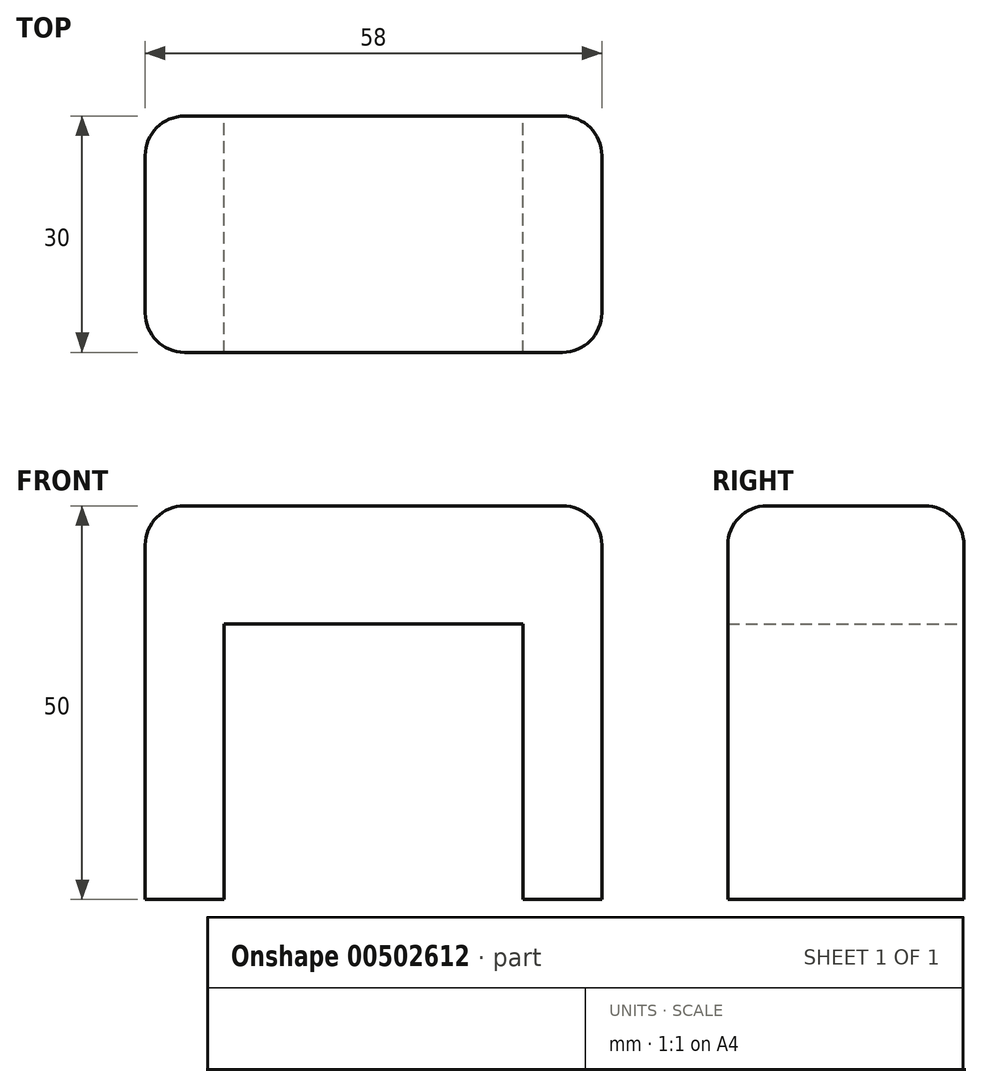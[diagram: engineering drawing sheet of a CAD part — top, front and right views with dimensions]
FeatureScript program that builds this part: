
annotation { "Feature Type Name" : "Feature", "Feature Type Description" : "" }
export const myFeature = defineFeature(function(context is Context, id is Id, definition is map)
    precondition{}
    {
        {
            var Q0;
            Q0=qCreatedBy(makeId("Front.planeOp"),FACE);
            var sketch = newSketch(context, id + "F0", { "sketchPlane" : qUnion([Q0])});
            skLineSegment(sketch, "E0.bottom", {"start": v(0, 0) * mm, "end": v(10, 0) * mm});
            skLineSegment(sketch, "E0.top", {"start": v(0, -50) * mm, "end": v(10, -50) * mm});
            skLineSegment(sketch, "E0.left", {"start": v(0, 0) * mm, "end": v(0, -50) * mm});
            skLineSegment(sketch, "E0.right", {"start": v(10, 0) * mm, "end": v(10, -50) * mm});
            skLineSegment(sketch, "E1.bottom", {"start": v(10, 0) * mm, "end": v(48, 0) * mm});
            skLineSegment(sketch, "E1.top", {"start": v(10, -15) * mm, "end": v(48, -15) * mm});
            skLineSegment(sketch, "E1.left", {"start": v(10, 0) * mm, "end": v(10, -15) * mm});
            skLineSegment(sketch, "E1.right", {"start": v(48, 0) * mm, "end": v(48, -15) * mm});
            skLineSegment(sketch, "E2.bottom", {"start": v(48, 0) * mm, "end": v(58, 0) * mm});
            skLineSegment(sketch, "E2.top", {"start": v(48, -50) * mm, "end": v(58, -50) * mm});
            skLineSegment(sketch, "E2.left", {"start": v(48, 0) * mm, "end": v(48, -50) * mm});
            skLineSegment(sketch, "E2.right", {"start": v(58, 0) * mm, "end": v(58, -50) * mm});
            skSolve(sketch);
        }
        {
            var Q0;
            Q0 = qSketchRegion(id + "F0", true);
            extrude(context, id + "F1", {"entities" : qUnion([Q0]), "depth" : 30 * mm});
        }
        {
            var Q0;
            Q0=makeQuery(id+"F1.opExtrude","SWEPT_FACE",FACE,{"disambiguationData":[OSD([sQuery(id+"F0.wireOp",EDGE,"E0.bottom"),sQuery(id+"F0.wireOp",EDGE,"E1.bottom"),sQuery(id+"F0.wireOp",EDGE,"E2.bottom")])]});
            var Q1;
            Q1=makeQuery(id+"F1.opExtrude","CAP_EDGE",EDGE,{"disambiguationData":[OSD([sQuery(id+"F0.wireOp",EDGE,"E0.left")])],"isStart":true});
            var Q2;
            Q2=makeQuery(id+"F1.opExtrude","CAP_EDGE",EDGE,{"disambiguationData":[OSD([sQuery(id+"F0.wireOp",EDGE,"E0.left")])],"isStart":false});
            var Q3;
            Q3=makeQuery(id+"F1.opExtrude","CAP_EDGE",EDGE,{"disambiguationData":[OSD([sQuery(id+"F0.wireOp",EDGE,"E2.right")])],"isStart":false});
            var Q4;
            Q4=makeQuery(id+"F1.opExtrude","CAP_EDGE",EDGE,{"disambiguationData":[OSD([sQuery(id+"F0.wireOp",EDGE,"E2.right")])],"isStart":true});
            fillet(context, id + "F2", {"entities" : qUnion([Q0, Q1, Q2, Q3, Q4]), "radius" : 5 * mm, "tangentPropagation" : true, "allowEdgeOverflow" : false});
        }
    });
